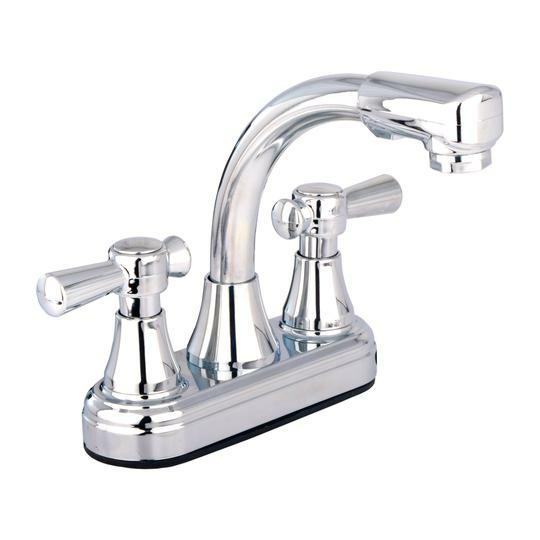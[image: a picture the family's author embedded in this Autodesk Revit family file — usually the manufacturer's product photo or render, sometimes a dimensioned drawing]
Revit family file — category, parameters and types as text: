
# Revit family: 01-1462-11 MEZCLADOR LAVAMANOS BAR 4” TOSCANA
name_source: partatom
category: Plumbing Fixtures
revit_build: Autodesk Revit 2018 (Build: 20170223_1515(x64)
units: mm (PartAtom-declared; Revit-internal decimal feet)

## family parameters
Cut with Voids When Loaded = No
Host = Face
OmniClass Number = 23.31.11.00
Part Type = Normal
Room Calculation Point = No
Round Connector Dimension = Use Diameter
Shared = No

## types (1)
- 01-1462-11
    Alto = 191.7 mm
    Alto Aireador = 160.5 mm
    Ancho brazo = 138.8 mm
    Ancho entre manijas = 101.6 mm  [stored 0.333333 ft]
    Ancho manija = 70 mm  [stored 0.229659 ft]
    CW Connection = Yes
    Default Elevation = 0 mm  [stored 0 ft]
    Description = Bimando
    HW Connection = Yes
    Link Ficha Tecnica = http://infotecnica.gricol.com
    Manufacturer = Gricol
    Model = 01-1462-11
    Plastico - ABS Cromado = Plastico - ABS Cromado
    Product Name = MEZCLADOR LAVAMANOS BAR 4” TOSCANA
    Type Image = MEZCLADOR LAVAMANOS BAR 4” TOSCANA.jpg
    URL = https://www.gricol.com
    Vent Connection = No
    Waste Connection = No

note: [stored X ft] marks values corroborated as IEEE doubles in the binary element streams (Revit-internal decimal feet)

## geometry (parser evidence)
native form markers: Blend x2, Sweep x2
no freeform markers — native parametric forms only
